# Revit family: 359748
name_source: partatom
category: Plumbing Fixtures
revit_build: Autodesk Revit 2013 (Build: 20120221_2030(x64)
units: mm (PartAtom-declared; Revit-internal decimal feet)

## types (1)
- 359748
    Assembly Code = D2090800
    CW Connection = Yes
    Calculation flow rate = DW 0,07 l/s, DWW 0,07 l/s
    Flow time = 1 - 15 adjustable
    HW Connection = Yes
    Manufacturer = FRANKE KITCHEN SYSTEMS (PTY) LTD
    Material = Chromium-plated Brass, Polished
    Minimum flow pressure = 1.0 Bar
    Model = Aquamix-C AQUA202 Self-Closing Hot and Cold Pillar Metering Tap
    Product Code = 359748
    Specification = For wash systems as a basin mixer with aerator with integrated flow controller. For connecting to the hot and cold water supply. Self-closing mixing cartridge, piston-free design, with automatic and backlash-free closure. Adjustable flow duration. With finely adjustable and twist-proof temperature stop. Full metal construction, polished chromium-plated brass. Optionally with connecting hoses or connecting pipes, connecting pieces with integrated non-return valves and dirt strainers.
    Vent Connection = No
    Volumetric flow = 0.10 l/s at a flow pressure of 3 bar
    Waste Connection = No

## geometry (parser evidence)
native form markers: Blend x4, Sweep x1
no freeform markers — native parametric forms only
